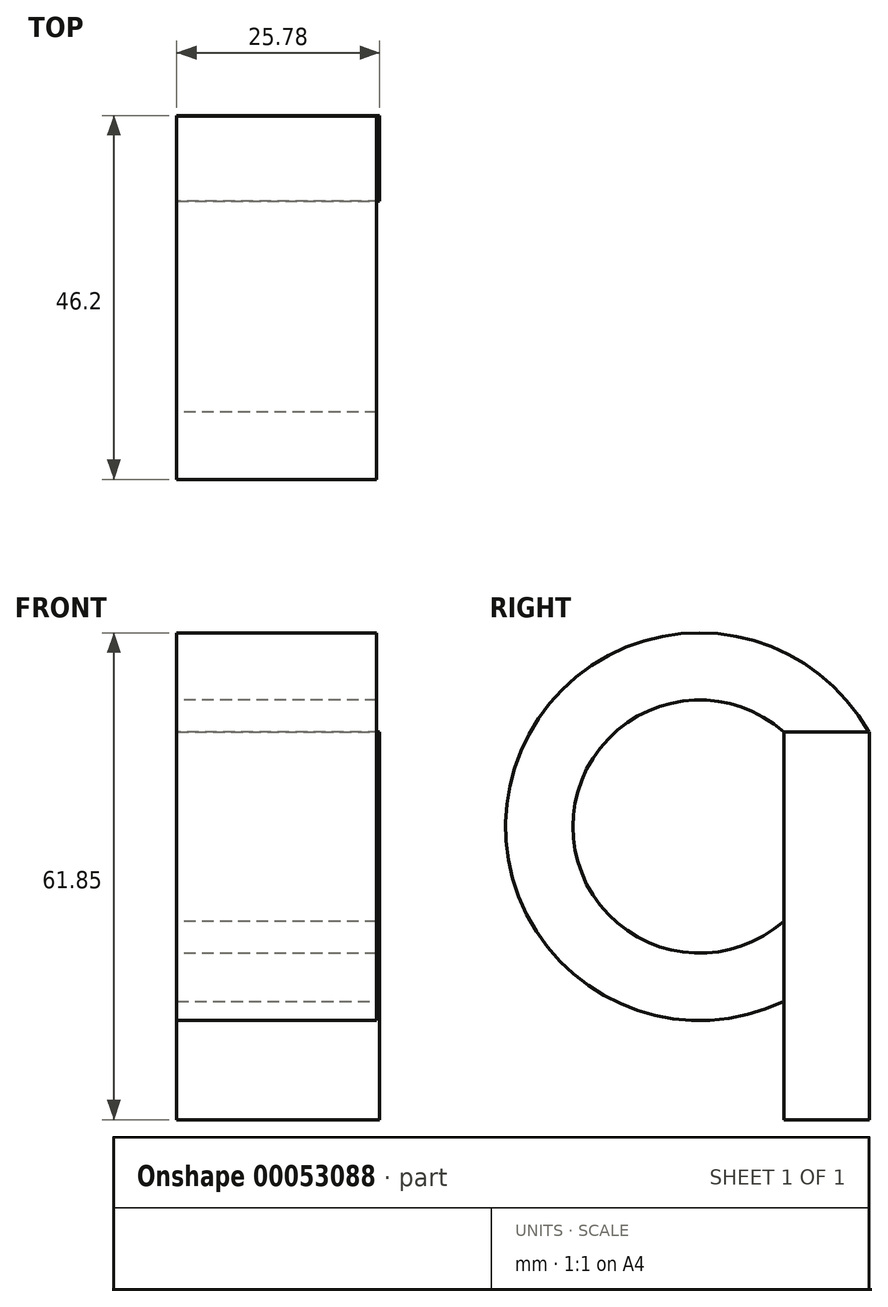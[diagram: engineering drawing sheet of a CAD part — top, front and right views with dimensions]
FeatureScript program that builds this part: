
annotation { "Feature Type Name" : "Feature", "Feature Type Description" : "" }
export const myFeature = defineFeature(function(context is Context, id is Id, definition is map)
    precondition{}
    {
        {
            var Q0;
            Q0=qCreatedBy(makeId("Right.planeOp"),FACE);
            var sketch = newSketch(context, id + "F0", { "sketchPlane" : qUnion([Q0])});
            skCircle(sketch, "E0", {"center": v(0, 37.22) * mm, "radius": 24.62 * mm});
            skSolve(sketch);
        }
        {
            var Q0;
            Q0=makeQuery(id+"F0.imprint","IMPRINT",FACE,{"disambiguationData":[TD([[makeQuery(id+"F0.imprint","IMPRINT",EDGE,{"derivedFrom":sQuery(id+"F0.wireOp",EDGE,"E0")}),1.0]])]});
            extrude(context, id + "F1", {"entities" : qUnion([Q0]), "oppositeDirection" : true, "depth" : 25.4 * mm});
        }
        {
            var Q0;
            Q0=makeQuery(id+"F1.opExtrude","CAP_FACE",FACE,{"disambiguationData":[OSD([sQuery(id+"F0.wireOp",EDGE,"E0")])],"isStart":false});
            var sketch = newSketch(context, id + "F2", { "sketchPlane" : qUnion([Q0])});
            skCircle(sketch, "E1", {"center": v(0, 37.22) * mm, "radius": 16.08 * mm});
            skSolve(sketch);
        }
        {
            var Q0;
            Q0=makeQuery(id+"F2.imprint","IMPRINT",FACE,{"disambiguationData":[TD([[makeQuery(id+"F2.imprint","IMPRINT",EDGE,{"derivedFrom":sQuery(id+"F2.wireOp",EDGE,"E1")}),1.0]])]});
            extrude(context, id + "F3", {"entities" : qUnion([Q0]), "operationType" : NewBodyOperationType.REMOVE, "endBound" : BoundingType.THROUGH_ALL, "oppositeDirection" : true, "depth" : 25.4 * mm});
        }
        {
            var Q0;
            Q0=makeQuery(id+"F1.opExtrude","CAP_FACE",FACE,{"disambiguationData":[OSD([sQuery(id+"F0.wireOp",EDGE,"E0")])],"isStart":false});
            var sketch = newSketch(context, id + "F4", { "sketchPlane" : qUnion([Q0])});
            skLineSegment(sketch, "E2.bottom", {"start": v(-10.7, 49.24) * mm, "end": v(-38.74, 49.24) * mm});
            skLineSegment(sketch, "E2.top", {"start": v(-10.7, 0) * mm, "end": v(-38.74, 0) * mm});
            skLineSegment(sketch, "E2.left", {"start": v(-10.7, 49.24) * mm, "end": v(-10.7, 0) * mm});
            skLineSegment(sketch, "E2.right", {"start": v(-38.74, 49.24) * mm, "end": v(-38.74, 0) * mm});
            skSolve(sketch);
        }
        {
            var Q0;
            Q0 = qSketchRegion(id + "F4", true);
            extrude(context, id + "F5", {"entities" : qUnion([Q0]), "operationType" : NewBodyOperationType.ADD, "oppositeDirection" : true, "depth" : 25.78 * mm});
        }
        {
            var Q0;
            Q0=makeQuery(id+"F5.opExtrude","SWEPT_FACE",FACE,{"disambiguationData":[OSD([sQuery(id+"F4.wireOp",EDGE,"E2.right")])]});
            extrude(context, id + "F6", {"entities" : qUnion([Q0]), "operationType" : NewBodyOperationType.REMOVE, "oppositeDirection" : true, "depth" : 17.15 * mm});
        }
    });
